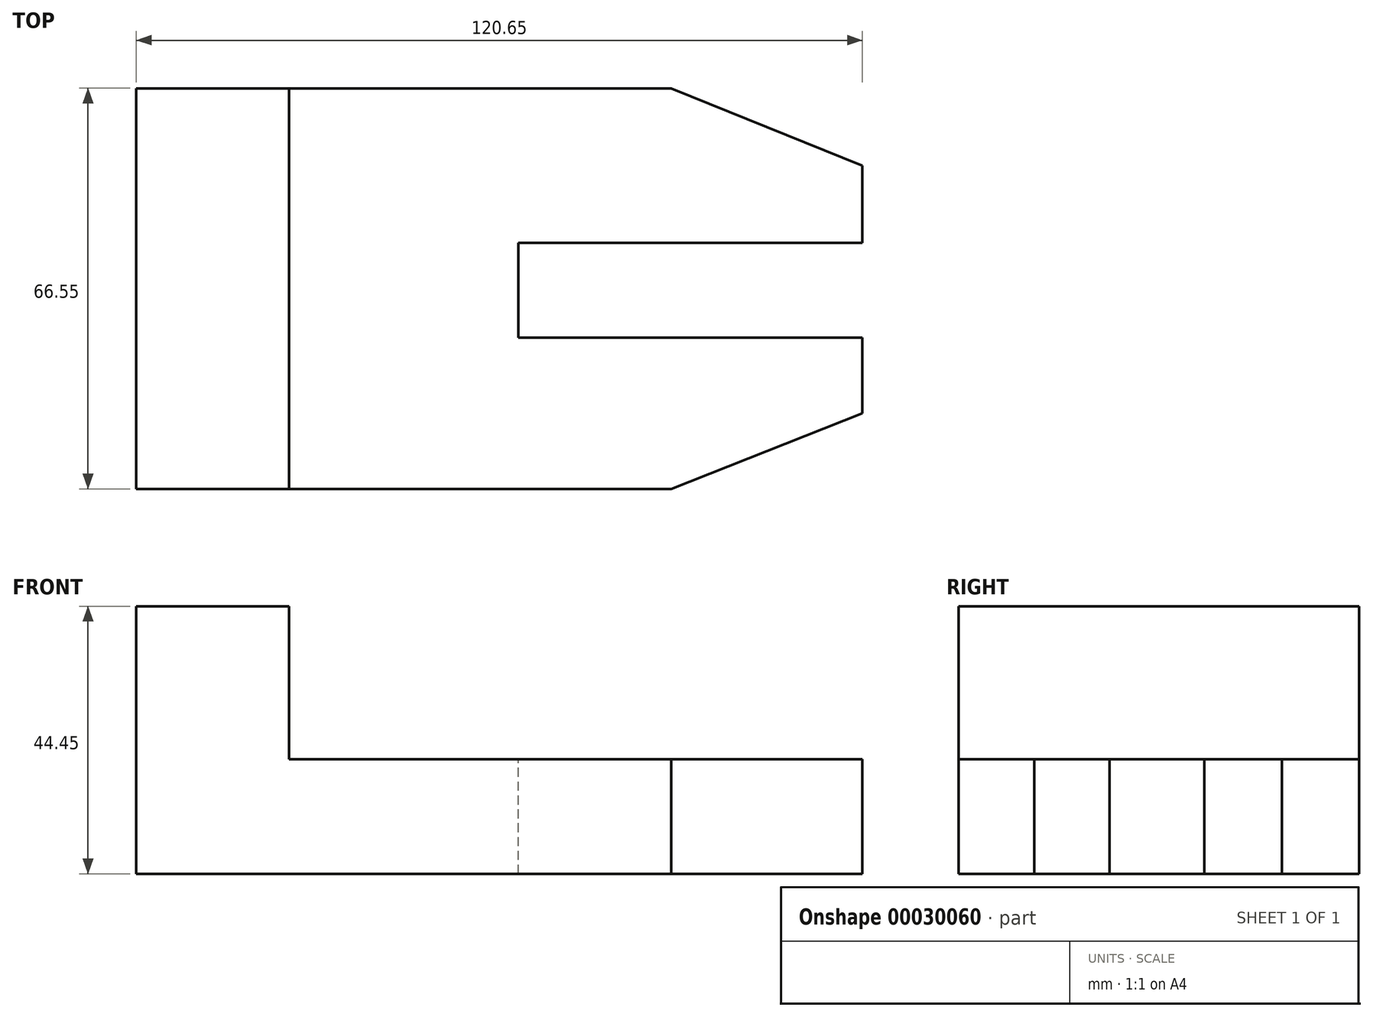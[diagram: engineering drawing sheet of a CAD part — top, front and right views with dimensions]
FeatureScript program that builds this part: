
annotation { "Feature Type Name" : "Feature", "Feature Type Description" : "" }
export const myFeature = defineFeature(function(context is Context, id is Id, definition is map)
    precondition{}
    {
        {
            var Q0;
            Q0=qCreatedBy(makeId("Front.planeOp"),FACE);
            var sketch = newSketch(context, id + "F0", { "sketchPlane" : qUnion([Q0])});
            skLineSegment(sketch, "E0", {"start": v(0, 0) * mm, "end": v(120.65, 0) * mm});
            skLineSegment(sketch, "E1", {"start": v(120.65, 0) * mm, "end": v(120.65, 19.05) * mm});
            skLineSegment(sketch, "E2", {"start": v(120.65, 19.05) * mm, "end": v(25.4, 19.05) * mm});
            skLineSegment(sketch, "E3", {"start": v(25.4, 19.05) * mm, "end": v(25.4, 44.45) * mm});
            skLineSegment(sketch, "E4", {"start": v(25.4, 44.45) * mm, "end": v(0, 44.45) * mm});
            skLineSegment(sketch, "E5", {"start": v(0, 44.45) * mm, "end": v(0, 0) * mm});
            skSolve(sketch);
        }
        {
            var Q0;
            Q0=makeQuery(id+"F0.imprint","IMPRINT",FACE,{"disambiguationData":[TD([[makeQuery(id+"F0.imprint","IMPRINT",EDGE,{"derivedFrom":sQuery(id+"F0.wireOp",EDGE,"E0")}),1.0]])]});
            extrude(context, id + "F1", {"entities" : qUnion([Q0]), "oppositeDirection" : true, "depth" : 66.55 * mm});
        }
        {
            var Q0;
            Q0=makeQuery(id+"F1.opExtrude","SWEPT_FACE",FACE,{"disambiguationData":[OSD([sQuery(id+"F0.wireOp",EDGE,"E2")])]});
            var sketch = newSketch(context, id + "F2", { "sketchPlane" : qUnion([Q0])});
            skLineSegment(sketch, "E6", {"start": v(120.65, 33.27) * mm, "end": v(63.5, 33.27) * mm});
            skLineSegment(sketch, "E7", {"start": v(63.5, 33.27) * mm, "end": v(63.5, 40.84) * mm});
            skLineSegment(sketch, "E8", {"start": v(63.5, 40.84) * mm, "end": v(120.65, 40.84) * mm});
            skLineSegment(sketch, "E9", {"start": v(63.5, 33.27) * mm, "end": v(63.5, 25.09) * mm});
            skLineSegment(sketch, "E10", {"start": v(63.5, 25.09) * mm, "end": v(120.65, 25.09) * mm});
            skLineSegment(sketch, "E11", {"start": v(120.65, 40.84) * mm, "end": v(120.65, 25.09) * mm});
            skSolve(sketch);
        }
        {
            var Q0;
            {var subQ2=sQuery(id+"F2.wireOp",EDGE,"E6");Q0=makeQuery(id+"F2.imprint","IMPRINT",FACE,{"disambiguationData":[TD([[makeQuery(id+"F2.imprint","IMPRINT",EDGE,{"derivedFrom":subQ2}),1.0]])]});}
            var Q1;
            {var subQ2=sQuery(id+"F2.wireOp",EDGE,"E6");Q1=makeQuery(id+"F2.imprint","IMPRINT",FACE,{"disambiguationData":[TD([[makeQuery(id+"F2.imprint","IMPRINT",EDGE,{"derivedFrom":subQ2}),-1.0]])]});}
            extrude(context, id + "F3", {"entities" : qUnion([Q0, Q1]), "operationType" : NewBodyOperationType.REMOVE, "endBound" : BoundingType.THROUGH_ALL, "oppositeDirection" : true, "depth" : 25.4 * mm});
        }
        {
            var Q0;
            Q0=makeQuery(id+"F1.opExtrude","SWEPT_FACE",FACE,{"disambiguationData":[OSD([sQuery(id+"F0.wireOp",EDGE,"E2")])]});
            var sketch = newSketch(context, id + "F4", { "sketchPlane" : qUnion([Q0])});
            skLineSegment(sketch, "E12", {"start": v(120.65, 0) * mm, "end": v(88.9, 0) * mm});
            skLineSegment(sketch, "E13", {"start": v(88.9, 0) * mm, "end": v(120.65, 12.54) * mm});
            skLineSegment(sketch, "E14", {"start": v(120.65, 12.54) * mm, "end": v(120.65, 0) * mm});
            skLineSegment(sketch, "E15", {"start": v(120.65, 66.55) * mm, "end": v(88.9, 66.55) * mm});
            skLineSegment(sketch, "E16", {"start": v(88.9, 66.55) * mm, "end": v(120.65, 53.7) * mm});
            skLineSegment(sketch, "E17", {"start": v(120.65, 53.7) * mm, "end": v(120.65, 66.55) * mm});
            skSolve(sketch);
        }
        {
            var Q0;
            Q0 = qSketchRegion(id + "F4", true);
            extrude(context, id + "F5", {"entities" : qUnion([Q0]), "operationType" : NewBodyOperationType.REMOVE, "endBound" : BoundingType.THROUGH_ALL, "oppositeDirection" : true, "depth" : 25.4 * mm});
        }
    });
